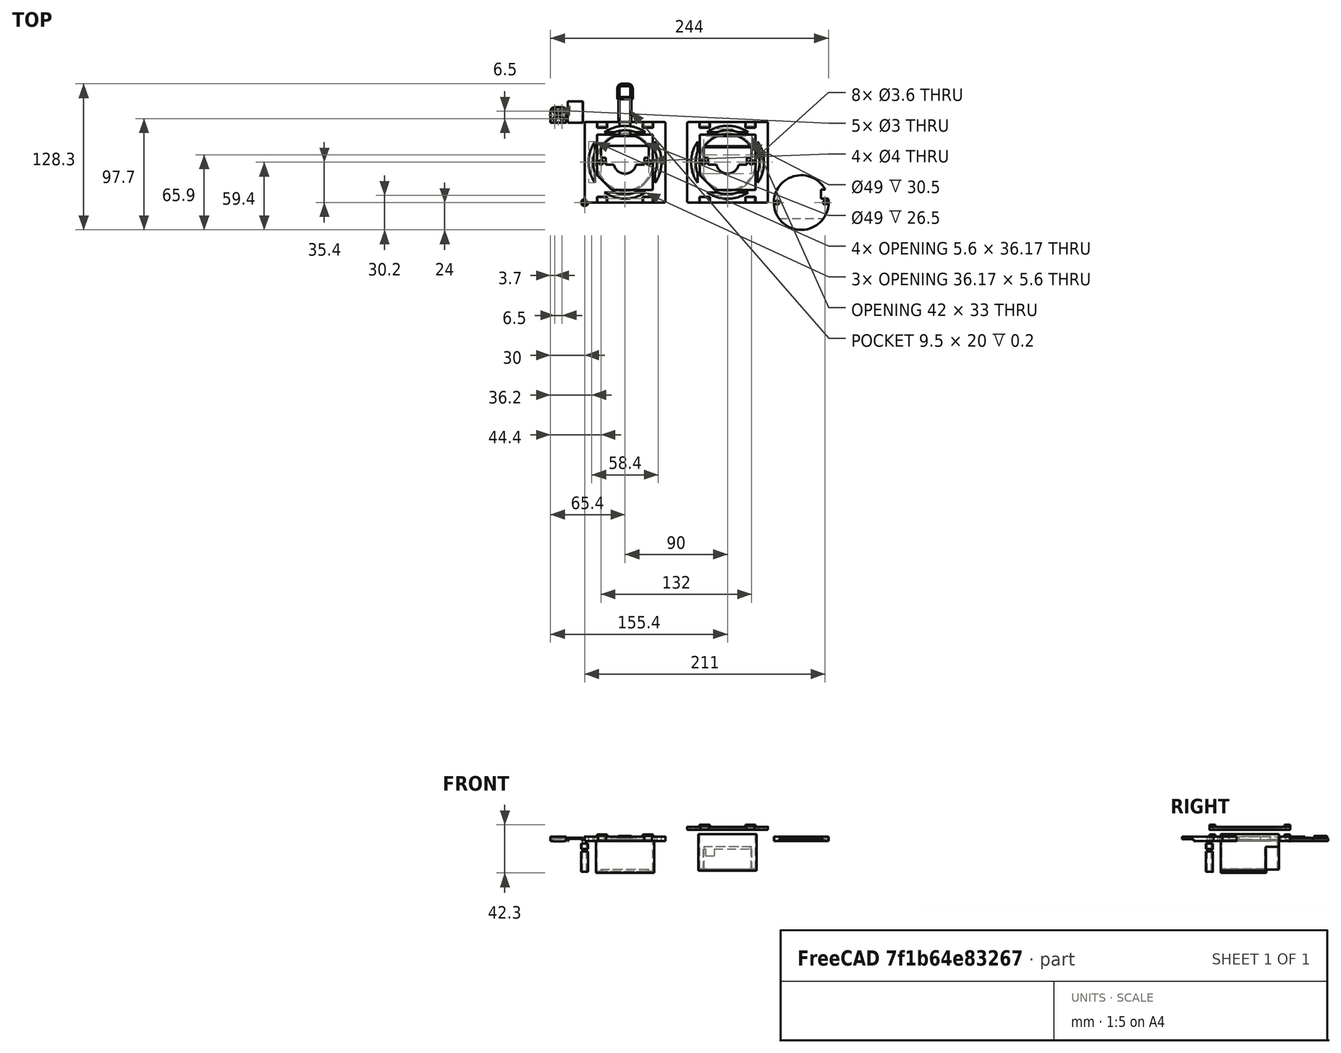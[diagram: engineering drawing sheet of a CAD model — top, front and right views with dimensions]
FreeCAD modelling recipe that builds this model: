
FCSTD DOCUMENT  (FreeCAD 0.19R24267 +99 (Git))
Label: TouchSwitchCase
License: All rights reserved
LicenseURL: http://en.wikipedia.org/wiki/All_rights_reserved
objects: Part::Box×43, Part::Cylinder×40, Part::Cut×35, Part::MultiFuse×22, Part::Fillet×7, Part::Chamfer×2, Part::MultiCommon×2
note: 151 computed .brp shape members not serialized (recipe doc carries the construction recipe); baked Part::Feature solids carry a one-line shape summary decoded from their .brp

FEATURE [Part::Box] Box  label="Base"
  AttacherType = Attacher::AttachEngine3D
  Height = 4
  Length = 70.8
  Width = 70.8
FEATURE [Part::Box] Box001  label="latch bottom left"
  AttacherType = Attacher::AttachEngine3D
  Height = 1.8
  Length = 9
  Placement = pos=(10.8,0,4) rot=(0,0,1;0rad)
  Width = 5
FEATURE [Part::Fillet] Fillet
  Base = -> Box
  Edges = 4 edges r=1: [Edge1,Edge3,Edge5,Edge7]
FEATURE [Part::Box] Box004  label="latch bottom right"
  AttacherType = Attacher::AttachEngine3D
  Height = 1.8
  Length = 9
  Placement = pos=(51,0,4) rot=(0,0,1;0rad)
  Width = 5
FEATURE [Part::Box] Box005  label="latch top left"
  AttacherType = Attacher::AttachEngine3D
  Height = 1.8
  Length = 9
  Placement = pos=(10.8,65.8,4) rot=(0,0,1;0rad)
  Width = 5
FEATURE [Part::Box] Box006  label="latch top right"
  AttacherType = Attacher::AttachEngine3D
  Height = 1.8
  Length = 9
  Placement = pos=(51,65.8,4) rot=(0,0,1;0rad)
  Width = 5
FEATURE [Part::Box] Box007  label="latch hole bottom left"
  AttacherType = Attacher::AttachEngine3D
  Height = 10
  Length = 7
  Placement = pos=(11.8,0,-5.2) rot=(0,0,1;0rad)
  Width = 4
FEATURE [Part::Box] Box008  label="latch hole bottom right"
  AttacherType = Attacher::AttachEngine3D
  Height = 10
  Length = 7
  Placement = pos=(52,0,-5.2) rot=(0,0,1;0rad)
  Width = 4
FEATURE [Part::Box] Box009  label="latch hole top left"
  AttacherType = Attacher::AttachEngine3D
  Height = 10
  Length = 7
  Placement = pos=(11.8,66.8,-5.2) rot=(0,0,1;0rad)
  Width = 4
FEATURE [Part::Box] Box010  label="latch hole top right"
  AttacherType = Attacher::AttachEngine3D
  Height = 10
  Length = 7
  Placement = pos=(52,66.8,-5.2) rot=(0,0,1;0rad)
  Width = 4
FEATURE [Part::Box] Box013  label="board holder hole"
  AttacherType = Attacher::AttachEngine3D
  Height = 10
  Length = 48.8
  Placement = pos=(11,11,0) rot=(0,0,1;0rad)
  Width = 48.8
FEATURE [Part::Chamfer] Chamfer
  Base = -> Box013
  Edges = 1 edges r=13: [Edge1]
  Placement = pos=(0,0,1.2) rot=(0,0,1;0rad)
FEATURE [Part::Cylinder] Cylinder  label="Central hole001"
  Angle = 360
  AttacherType = Attacher::AttachEngine3D
  Height = 40
  Placement = pos=(35.4,35.4,-10) rot=(0,0,1;0rad)
  Radius = 10
FEATURE [Part::Cylinder] Cylinder001  label="Left screw hole"
  Angle = 360
  AttacherType = Attacher::AttachEngine3D
  Height = 10
  Placement = pos=(5.4,35.4,-4) rot=(0,0,1;0rad)
  Radius = 2
FEATURE [Part::Cylinder] Cylinder002  label="Bottom screw hole"
  Angle = 360
  AttacherType = Attacher::AttachEngine3D
  Height = 10
  Placement = pos=(35.4,5.4,-4) rot=(0,0,1;0rad)
  Radius = 2
FEATURE [Part::Cylinder] Cylinder003  label="right screw hole"
  Angle = 360
  AttacherType = Attacher::AttachEngine3D
  Height = 10
  Placement = pos=(65.4,35.4,-4) rot=(0,0,1;0rad)
  Radius = 2
FEATURE [Part::Cylinder] Cylinder004  label="top screw hole"
  Angle = 360
  AttacherType = Attacher::AttachEngine3D
  Height = 10
  Placement = pos=(35.4,65.4,-4) rot=(0,0,1;0rad)
  Radius = 2
FEATURE [Part::Box] Box014  label="Connector hole"
  AttacherType = Attacher::AttachEngine3D
  Height = 10
  Length = 42
  Placement = pos=(14.4,39.4,-3) rot=(0,0,1;0rad)
  Width = 19
FEATURE [Part::Cylinder] Cylinder007  label="board hole left"
  Angle = 360
  AttacherType = Attacher::AttachEngine3D
  Height = 10
  Placement = pos=(14.4,35.4,-2) rot=(0,0,1;0rad)
  Radius = 2
FEATURE [Part::Cylinder] Cylinder009  label="Board hole right"
  Angle = 360
  AttacherType = Attacher::AttachEngine3D
  Height = 10
  Placement = pos=(56.4,35.4,-2) rot=(0,0,1;0rad)
  Radius = 2
FEATURE [Part::Box] Box015  label="Куб"
  AttacherType = Attacher::AttachEngine3D
  Height = 10
  Length = 34
  Placement = pos=(18.4,33.4,-2) rot=(0,0,1;0rad)
  Width = 10
FEATURE [Part::Cut] Cut
  Base = -> Fillet
  Tool = -> Chamfer
FEATURE [Part::Cut] Cut021
  Base = -> Cut
  Tool = -> Cylinder
FEATURE [Part::MultiFuse] Fusion004
  Shapes = -> [Box007,Box008,Box010,Box009]
FEATURE [Part::MultiFuse] Fusion005
  Shapes = -> [Fusion004]
FEATURE [Part::MultiFuse] Fusion006
  Shapes = -> [Cylinder001,Cylinder004,Cylinder002,Cylinder003]
FEATURE [Part::Cylinder] Cylinder010  label="BodyBase"
  Angle = 360
  AttacherType = Attacher::AttachEngine3D
  Height = 28
  Radius = 25.5
FEATURE [Part::Cylinder] Cylinder011  label="BodyHole"
  Angle = 360
  AttacherType = Attacher::AttachEngine3D
  Height = 50
  Placement = pos=(0,0,1.5) rot=(0,0,1;0rad)
  Radius = 24.5
FEATURE [Part::Cylinder] Cylinder012  label="Цилиндр"
  Angle = 360
  AttacherType = Attacher::AttachEngine3D
  Height = 50
  Placement = pos=(-21,0,-5) rot=(0,0,1;0rad)
  Radius = 1.8
FEATURE [Part::Cut] Cut028
  Base = -> Cylinder010
  Tool = -> Cylinder011
FEATURE [Part::Cylinder] Cylinder013  label="Цилиндр001"
  Angle = 360
  AttacherType = Attacher::AttachEngine3D
  Height = 50
  Placement = pos=(21,0,-5) rot=(0,0,1;0rad)
  Radius = 1.8
FEATURE [Part::MultiFuse] Fusion008
  Shapes = -> [Cylinder012,Cylinder013]
FEATURE [Part::Cut] Cut029
  Base = -> Cut028
  Tool = -> Fusion008
FEATURE [Part::Box] Box016  label="Куб001"
  AttacherType = Attacher::AttachEngine3D
  Height = 10
  Length = 50
  Placement = pos=(-25,14.5,-7) rot=(0,0,1;0rad)
  Width = 15
FEATURE [Part::Cut] Cut030  label="Body"
  Base = -> Cut029
  Placement = pos=(35.4,35.4,-28) rot=(0,0,1;0rad)
  Tool = -> Box016
FEATURE [Part::Cylinder] Cylinder014  label="Цилиндр002"
  Angle = 360
  AttacherType = Attacher::AttachEngine3D
  Height = 30
  Placement = pos=(0,0,-3) rot=(0,0,1;0rad)
  Radius = 1.8
FEATURE [Part::Cylinder] Cylinder015  label="Цилиндр003"
  Angle = 360
  AttacherType = Attacher::AttachEngine3D
  Height = 18
  Radius = 3
FEATURE [Part::Cut] Cut031  label="PwrStand"
  Base = -> Cylinder015
  Placement = pos=(0,0,-27) rot=(0,0,1;0rad)
  Tool = -> Cylinder014
FEATURE [Part::Cylinder] Cylinder016  label="Цилиндр004"
  Angle = 360
  AttacherType = Attacher::AttachEngine3D
  Height = 20
  Placement = pos=(0,0,-3) rot=(0,0,1;0rad)
  Radius = 1.8
FEATURE [Part::Cylinder] Cylinder017  label="Цилиндр005"
  Angle = 360
  AttacherType = Attacher::AttachEngine3D
  Height = 4.8
  Radius = 3
FEATURE [Part::Cut] Cut032  label="TouchStand"
  Base = -> Cylinder017
  Placement = pos=(0,0,-7) rot=(0,0,1;0rad)
  Tool = -> Cylinder016
FEATURE [Part::MultiFuse] Fusion009
  Shapes = -> [Cylinder007,Cylinder009]
FEATURE [Part::MultiFuse] Fusion010
  Shapes = -> [Box015,Box014]
FEATURE [Part::Cylinder] Cylinder018  label="BodyHole001"
  Angle = 360
  AttacherType = Attacher::AttachEngine3D
  Height = 50
  Placement = pos=(35.4,35.4,-10.5) rot=(0,0,1;0rad)
  Radius = 24.5
FEATURE [Part::MultiFuse] Fusion
  Shapes = -> [Box001,Box004,Box005,Box006]
FEATURE [Part::MultiCommon] Common
  Shapes = -> [Fusion010,Cylinder018]
FEATURE [Part::Cut] Cut033
  Base = -> Cut021
  Tool = -> Fusion006
FEATURE [Part::Cut] Cut034
  Base = -> Cut033
  Tool = -> Fusion009
FEATURE [Part::MultiFuse] Fusion011
  Shapes = -> [Cut034,Fusion]
FEATURE [Part::Cut] Cut035
  Base = -> Fusion011
  Tool = -> Fusion005
FEATURE [Part::Cut] Cut036  label="Cap"
  Base = -> Cut035
  Tool = -> Common
FEATURE [Part::Box] Box017  label="Куб002"
  AttacherType = Attacher::AttachEngine3D
  Height = 2.5
  Length = 11.5
  Width = 22
FEATURE [Part::Box] Box018  label="Куб003"
  AttacherType = Attacher::AttachEngine3D
  Height = 10
  Length = 9.5
  Placement = pos=(1,0,1) rot=(0,0,1;0rad)
  Width = 30
FEATURE [Part::Cut] Cut037
  Base = -> Box017
  Placement = pos=(29.65,70.8,0) rot=(0,0,1;0rad)
  Tool = -> Box018
FEATURE [Part::Box] Box022  label="Куб007"
  AttacherType = Attacher::AttachEngine3D
  Height = 10
  Length = 9.5
  Placement = pos=(30.65,35,1.2) rot=(0,0,1;0rad)
  Width = 66
FEATURE [Part::Cylinder] Cylinder029  label="Цилиндр016"
  Angle = 360
  AttacherType = Attacher::AttachEngine3D
  Height = 10
  Placement = pos=(35.4,35.4,0) rot=(0,0,1;0rad)
  Radius = 32
FEATURE [Part::Cylinder] Cylinder030  label="Цилиндр017"
  Angle = 360
  AttacherType = Attacher::AttachEngine3D
  Height = 30
  Placement = pos=(35.4,35.4,-5) rot=(0,0,1;0rad)
  Radius = 28
FEATURE [Part::Cut] Cut045
  Base = -> Cylinder029
  Tool = -> Cylinder030
FEATURE [Part::Box] Box034  label="Куб021"
  AttacherType = Attacher::AttachEngine3D
  Height = 30
  Length = 52.8
  Placement = pos=(9,9,-5) rot=(0,0,1;0rad)
  Width = 52.8
FEATURE [Part::Cut] Cut046
  Base = -> Cut045
  Tool = -> Box034
FEATURE [Part::Cut] Cut047
  Base = -> Cut036
  Tool = -> Cut046
FEATURE [Part::Box] Box038  label="Куб025"
  AttacherType = Attacher::AttachEngine3D
  Height = 30
  Length = 9.5
  Placement = pos=(2,2,1) rot=(0,0,1;0rad)
  Width = 9.5
FEATURE [Part::Box] Box039  label="Куб026"
  AttacherType = Attacher::AttachEngine3D
  Height = 4.5
  Length = 11.5
  Placement = pos=(1,1,0) rot=(0,0,1;0rad)
  Width = 11.5
FEATURE [Part::Box] Box040  label="Куб027"
  AttacherType = Attacher::AttachEngine3D
  Height = 2.5
  Length = 13.5
  Width = 13.5
FEATURE [Part::Fillet] Fillet007
  Base = -> Box040
  Edges = 2 edges r=4: [Edge3,Edge7]
FEATURE [Part::Fillet] Fillet008
  Base = -> Box039
  Edges = 2 edges r=3: [Edge3,Edge7]
FEATURE [Part::Fillet] Fillet009
  Base = -> Box038
  Edges = 2 edges r=2: [Edge3,Edge7]
FEATURE [Part::MultiFuse] Fusion019
  Shapes = -> [Fillet007,Fillet008]
FEATURE [Part::Cut] Cut049  label="TempV2"
  Base = -> Fusion019
  Placement = pos=(28.65,90.8,0) rot=(0,0,1;0rad)
  Tool = -> Fillet009
FEATURE [Part::Box] Box041  label="Куб028"
  AttacherType = Attacher::AttachEngine3D
  Height = 4
  Length = 13.9
  Width = 13.9
FEATURE [Part::Fillet] Fillet010
  Base = -> Box041
  Edges = 2 edges r=4: [Edge3,Edge7]
FEATURE [Part::Box] Box042  label="Куб029"
  AttacherType = Attacher::AttachEngine3D
  Height = 2
  Length = 11.9
  Placement = pos=(1,1,0) rot=(0,0,1;0rad)
  Width = 11.9
FEATURE [Part::Fillet] Fillet011
  Base = -> Box042
  Edges = 2 edges r=3: [Edge3,Edge7]
FEATURE [Part::Cut] Cut051
  Base = -> Fillet010
  Tool = -> Fillet011
FEATURE [Part::Cylinder] Cylinder031  label="Цилиндр018"
  Angle = 360
  AttacherType = Attacher::AttachEngine3D
  Height = 10
  Placement = pos=(6.95,6.95,0) rot=(0,0,1;0rad)
  Radius = 1.5
FEATURE [Part::Cylinder] Cylinder032  label="Цилиндр019"
  Angle = 360
  AttacherType = Attacher::AttachEngine3D
  Height = 10
  Placement = pos=(3.7,3.7,0) rot=(0,0,1;0rad)
  Radius = 1.5
FEATURE [Part::Cylinder] Cylinder033  label="Цилиндр020"
  Angle = 360
  AttacherType = Attacher::AttachEngine3D
  Height = 10
  Placement = pos=(3.7,10.2,0) rot=(0,0,1;0rad)
  Radius = 1.5
FEATURE [Part::Cylinder] Cylinder034  label="Цилиндр021"
  Angle = 360
  AttacherType = Attacher::AttachEngine3D
  Height = 10
  Placement = pos=(10.2,3.7,0) rot=(0,0,1;0rad)
  Radius = 1.5
FEATURE [Part::Cylinder] Cylinder035  label="Цилиндр022"
  Angle = 360
  AttacherType = Attacher::AttachEngine3D
  Height = 10
  Placement = pos=(10.2,10.2,0) rot=(0,0,1;0rad)
  Radius = 1.5
FEATURE [Part::MultiFuse] Fusion021
  Shapes = -> [Cylinder032,Cylinder033,Cylinder031,Cylinder035,Cylinder034]
FEATURE [Part::Cut] Cut052
  Base = -> Cut051
  Tool = -> Fusion021
FEATURE [Part::MultiFuse] Fusion022
  Shapes = -> [Cut047,Cut037,Cut049]
FEATURE [Part::Cut] Cut053  label="MeteoCup"
  Base = -> Fusion022
  Tool = -> Box022
FEATURE [Part::Box] Box043  label="Куб030"
  AttacherType = Attacher::AttachEngine3D
  Height = 2
  Length = 9.3
  Placement = pos=(2.3,0,-0.4) rot=(0,0,1;0rad)
  Width = 1
FEATURE [Part::MultiFuse] Fusion023  label="SensorCap"
  Placement = pos=(-30,70,0) rot=(0,0,1;0rad)
  Shapes = -> [Cut052,Box043]
FEATURE [Part::Box] Box044  label="Куб031"
  AttacherType = Attacher::AttachEngine3D
  Height = 3
  Length = 13.5
  Width = 19
FEATURE [Part::Box] Box045  label="Куб032"
  AttacherType = Attacher::AttachEngine3D
  Height = 2
  Length = 11.9
  Placement = pos=(0.8,0,0) rot=(0,0,1;0rad)
  Width = 20
FEATURE [Part::Cut] Cut054  label="CableCup"
  Base = -> Box044
  Placement = pos=(-15,70,0) rot=(0,0,1;0rad)
  Tool = -> Box045
FEATURE [Part::Box] Box029  label="Base001"
  AttacherType = Attacher::AttachEngine3D
  Height = 2.5
  Length = 70.8
  Width = 70.8
FEATURE [Part::Fillet] Fillet001
  Base = -> Box029
  Edges = 4 edges r=1: [Edge1,Edge3,Edge5,Edge7]
FEATURE [Part::Box] Box026  label="latch hole bottom left001"
  AttacherType = Attacher::AttachEngine3D
  Height = 10
  Length = 7
  Placement = pos=(11.8,0,-6.7) rot=(0,0,1;0rad)
  Width = 4
FEATURE [Part::Cylinder] Cylinder022  label="Central hole002"
  Angle = 360
  AttacherType = Attacher::AttachEngine3D
  Height = 40
  Placement = pos=(35.4,35.4,-10) rot=(0,0,1;0rad)
  Radius = 10
FEATURE [Part::Box] Box024  label="latch top left001"
  AttacherType = Attacher::AttachEngine3D
  Height = 1.8
  Length = 9
  Placement = pos=(10.8,65.8,2.5) rot=(0,0,1;0rad)
  Width = 5
FEATURE [Part::Box] Box021  label="latch bottom left001"
  AttacherType = Attacher::AttachEngine3D
  Height = 1.8
  Length = 9
  Placement = pos=(10.8,0,2.5) rot=(0,0,1;0rad)
  Width = 5
FEATURE [Part::Box] Box031  label="Connector hole001"
  AttacherType = Attacher::AttachEngine3D
  Height = 10
  Length = 42
  Placement = pos=(14.4,39.4,-3) rot=(0,0,1;0rad)
  Width = 19
FEATURE [Part::Box] Box032  label="Куб006"
  AttacherType = Attacher::AttachEngine3D
  Height = 10
  Length = 34
  Placement = pos=(18.4,33.4,-2) rot=(0,0,1;0rad)
  Width = 10
FEATURE [Part::MultiFuse] Fusion020
  Shapes = -> [Box032,Box031]
FEATURE [Part::Cylinder] Cylinder027  label="board hole left001"
  Angle = 360
  AttacherType = Attacher::AttachEngine3D
  Height = 10
  Placement = pos=(14.4,35.4,-2) rot=(0,0,1;0rad)
  Radius = 2
FEATURE [Part::Box] Box023  label="latch hole top right001"
  AttacherType = Attacher::AttachEngine3D
  Height = 10
  Length = 7
  Placement = pos=(52,66.8,-6.7) rot=(0,0,1;0rad)
  Width = 4
FEATURE [Part::Box] Box046  label="latch top right001"
  AttacherType = Attacher::AttachEngine3D
  Height = 1.8
  Length = 9
  Placement = pos=(51,65.8,2.5) rot=(0,0,1;0rad)
  Width = 5
FEATURE [Part::Box] Box027  label="latch hole bottom right001"
  AttacherType = Attacher::AttachEngine3D
  Height = 10
  Length = 7
  Placement = pos=(52,0,-6.7) rot=(0,0,1;0rad)
  Width = 4
FEATURE [Part::Box] Box025  label="latch bottom right001"
  AttacherType = Attacher::AttachEngine3D
  Height = 1.8
  Length = 9
  Placement = pos=(51,0,2.5) rot=(0,0,1;0rad)
  Width = 5
FEATURE [Part::MultiFuse] Fusion016
  Shapes = -> [Box021,Box025,Box024,Box046]
FEATURE [Part::Box] Box028  label="latch hole top left001"
  AttacherType = Attacher::AttachEngine3D
  Height = 10
  Length = 7
  Placement = pos=(11.8,66.8,-6.7) rot=(0,0,1;0rad)
  Width = 4
FEATURE [Part::MultiFuse] Fusion014
  Shapes = -> [Box026,Box027,Box023,Box028]
FEATURE [Part::MultiFuse] Fusion015
  Shapes = -> [Fusion014]
FEATURE [Part::Box] Box030  label="board holder hole001"
  AttacherType = Attacher::AttachEngine3D
  Height = 10
  Length = 48.8
  Placement = pos=(11,11,0) rot=(0,0,1;0rad)
  Width = 48.8
FEATURE [Part::Chamfer] Chamfer001
  Base = -> Box030
  Edges = 1 edges r=13: [Edge1]
  Placement = pos=(0,0,1.2) rot=(0,0,1;0rad)
FEATURE [Part::Cut] Cut040
  Base = -> Fillet001
  Tool = -> Chamfer001
FEATURE [Part::Cut] Cut041
  Base = -> Cut040
  Tool = -> Cylinder022
FEATURE [Part::Cylinder] Cylinder024  label="Board hole right001"
  Angle = 360
  AttacherType = Attacher::AttachEngine3D
  Height = 10
  Placement = pos=(56.4,35.4,-2) rot=(0,0,1;0rad)
  Radius = 2
FEATURE [Part::MultiFuse] Fusion017
  Shapes = -> [Cylinder027,Cylinder024]
FEATURE [Part::Cylinder] Cylinder023  label="Bottom screw hole001"
  Angle = 360
  AttacherType = Attacher::AttachEngine3D
  Height = 10
  Placement = pos=(35.4,5.4,-4) rot=(0,0,1;0rad)
  Radius = 2
FEATURE [Part::Cylinder] Cylinder025  label="Left screw hole001"
  Angle = 360
  AttacherType = Attacher::AttachEngine3D
  Height = 10
  Placement = pos=(5.4,35.4,-4) rot=(0,0,1;0rad)
  Radius = 2
FEATURE [Part::Cylinder] Cylinder026  label="right screw hole001"
  Angle = 360
  AttacherType = Attacher::AttachEngine3D
  Height = 10
  Placement = pos=(65.4,35.4,-4) rot=(0,0,1;0rad)
  Radius = 2
FEATURE [Part::Cylinder] Cylinder028  label="top screw hole001"
  Angle = 360
  AttacherType = Attacher::AttachEngine3D
  Height = 10
  Placement = pos=(35.4,65.4,-4) rot=(0,0,1;0rad)
  Radius = 2
FEATURE [Part::MultiFuse] Fusion018
  Shapes = -> [Cylinder025,Cylinder028,Cylinder023,Cylinder026]
FEATURE [Part::Cut] Cut042
  Base = -> Cut041
  Tool = -> Fusion018
FEATURE [Part::Cut] Cut048
  Base = -> Cut042
  Tool = -> Fusion017
FEATURE [Part::MultiFuse] Fusion024
  Shapes = -> [Cut048,Fusion016]
FEATURE [Part::Cut] Cut043
  Base = -> Fusion024
  Tool = -> Fusion015
FEATURE [Part::Cylinder] Cylinder036  label="Цилиндр023"
  Angle = 360
  AttacherType = Attacher::AttachEngine3D
  Height = 10
  Placement = pos=(35.4,35.4,0) rot=(0,0,1;0rad)
  Radius = 32
FEATURE [Part::Cylinder] Cylinder037  label="Цилиндр024"
  Angle = 360
  AttacherType = Attacher::AttachEngine3D
  Height = 30
  Placement = pos=(35.4,35.4,-5) rot=(0,0,1;0rad)
  Radius = 28
FEATURE [Part::Cut] Cut056
  Base = -> Cylinder036
  Tool = -> Cylinder037
FEATURE [Part::Cylinder] Cylinder038  label="BodyHole002"
  Angle = 360
  AttacherType = Attacher::AttachEngine3D
  Height = 50
  Placement = pos=(35.4,35.4,-10.5) rot=(0,0,1;0rad)
  Radius = 24.5
FEATURE [Part::MultiCommon] Common001
  Shapes = -> [Fusion020,Cylinder038]
FEATURE [Part::Cut] Cut044  label="Cap001"
  Base = -> Cut043
  Tool = -> Common001
FEATURE [Part::Box] Box047  label="Куб033"
  AttacherType = Attacher::AttachEngine3D
  Height = 30
  Length = 52.8
  Placement = pos=(9,9,-5) rot=(0,0,1;0rad)
  Width = 52.8
FEATURE [Part::Cut] Cut057
  Base = -> Cut056
  Tool = -> Box047
FEATURE [Part::Cut] Cut055  label="BodyCup"
  Base = -> Cut044
  Placement = pos=(90,0,10) rot=(0,0,1;0rad)
  Tool = -> Cut057
FEATURE [Part::Cylinder] Cylinder039  label="Цилиндр025"
  Angle = 360
  AttacherType = Attacher::AttachEngine3D
  Height = 50
  Placement = pos=(21,0,-5) rot=(0,0,1;0rad)
  Radius = 1.8
FEATURE [Part::Box] Box048  label="Куб034"
  AttacherType = Attacher::AttachEngine3D
  Height = 30
  Length = 50
  Placement = pos=(-25,14,-9) rot=(0,0,1;0rad)
  Width = 15
FEATURE [Part::Box] Box020  label="Куб005"
  AttacherType = Attacher::AttachEngine3D
  Height = 7
  Length = 7.5
  Placement = pos=(16.2,44,-13) rot=(0,0,1;0rad)
  Width = 10
FEATURE [Part::Box] Box019  label="Куб004"
  AttacherType = Attacher::AttachEngine3D
  Height = 18.5
  Length = 42
  Placement = pos=(14.5,48.5,-25.5) rot=(0,0,1;0rad)
  Width = 1
FEATURE [Part::Cut] Cut039
  Base = -> Box019
  Tool = -> Box020
FEATURE [Part::Box] Box049  label="Куб035"
  AttacherType = Attacher::AttachEngine3D
  Height = 1.5
  Length = 60
  Placement = pos=(-30,-24,0) rot=(0,0,1;0rad)
  Width = 10
FEATURE [Part::Box] Box050  label="Куб036"
  AttacherType = Attacher::AttachEngine3D
  Height = 10
  Length = 24
  Placement = pos=(17.5,3.5,-3) rot=(0,0,1;0rad)
  Width = 8
FEATURE [Part::Cylinder] Cylinder040  label="BodyHole003"
  Angle = 360
  AttacherType = Attacher::AttachEngine3D
  Height = 50
  Placement = pos=(0,0,1.5) rot=(0,0,1;0rad)
  Radius = 24.5
FEATURE [Part::Cylinder] Cylinder041  label="Цилиндр026"
  Angle = 360
  AttacherType = Attacher::AttachEngine3D
  Height = 50
  Placement = pos=(-21,0,-5) rot=(0,0,1;0rad)
  Radius = 1.8
FEATURE [Part::MultiFuse] Fusion025
  Shapes = -> [Cylinder041,Cylinder039]
FEATURE [Part::Cylinder] Cylinder042  label="BodyBase001"
  Angle = 360
  AttacherType = Attacher::AttachEngine3D
  Height = 32
  Radius = 25.5
FEATURE [Part::Cut] Cut061
  Base = -> Cylinder042
  Tool = -> Cylinder040
FEATURE [Part::Cut] Cut059
  Base = -> Cut061
  Tool = -> Fusion025
FEATURE [Part::Cut] Cut060  label="Body001"
  Base = -> Cut059
  Placement = pos=(35.4,35.4,-26) rot=(0,0,1;0rad)
  Tool = -> Box048
FEATURE [Part::MultiFuse] Fusion013  label="BodyV2"
  Placement = pos=(90,0,0) rot=(0,0,1;0rad)
  Shapes = -> [Cut039,Cut060]
FEATURE [Part::Cylinder] Cylinder019  label="Цилиндр006"
  Angle = 360
  AttacherType = Attacher::AttachEngine3D
  Height = 4
  Radius = 24
FEATURE [Part::Cylinder] Cylinder020  label="Цилиндр007"
  Angle = 360
  AttacherType = Attacher::AttachEngine3D
  Height = 20
  Placement = pos=(-21,0,-3) rot=(0,0,1;0rad)
  Radius = 1.8
FEATURE [Part::Cylinder] Cylinder021  label="Цилиндр008"
  Angle = 360
  AttacherType = Attacher::AttachEngine3D
  Height = 20
  Placement = pos=(21,0,-3) rot=(0,0,1;0rad)
  Radius = 1.8
FEATURE [Part::MultiFuse] Fusion012
  Shapes = -> [Cylinder020,Cylinder021,Box049]
FEATURE [Part::Cut] Cut058
  Base = -> Cylinder019
  Tool = -> Fusion012
FEATURE [Part::Cut] Cut038
  Base = -> Cut058
  Placement = pos=(190,0,0) rot=(0,0,1;0rad)
  Tool = -> Box050
